# Revit family: 6218_Lange Gewindetülle mit Konus
name_source: partatom
category: Rohrformteile
units: mm (PartAtom-declared; Revit-internal decimal feet)

## family parameters
Arbeitsebenenbasiert = Nein
Beim Laden mit Abzugskörper schneiden = Nein
Bemaßung runder Anschluss = Durchmesser verwenden
Gemeinsam genutzt = Nein
Immer vertikal = Ja
OmniClass-Nummer = 23.65.55.14
OmniClass-Titel = Valves for Liquid Services
Teiletyp = Verbindung

## types (3) — shared parameters
Ausführung = Lange Gewindetülle, ohne Mutter, mit Konus, zum ausgleichen von Baumaßdifferenzen
Gewindetülle = Messing CW614N, vernickelt
Hersteller = HERZ Armaturen Ges.m.b.H.
Hinweiß = Der O-Ring dient als zusätzliche Dichtung, bei Verlust ist die Gewindetülle metallisch dichtend.
L02 = 3 mm  [stored 0.00984252 ft]
Max. Betriebsdruck = 1000000.0 Pa
Max. Betriebstemperatur = 110 °C
Medium = Heizungswasser nach ÖNORM H5195 oder VDI- Richtlinie 2035.
Die Verwendung von Ethylen- oder Propyleneglykol in einem Mischungsverhältnis 25- 50% ist zulässig.
O-Ring = EPDM
SCRNCODE = 07;01;01
SCRNSEQ = AWI;AWI_TYP="1001";1
URL = www.herz-armaturen.at
zero-valued in all types: Vorgabe-Ansicht

## per-type parameters (varying)
| type | D00 | D01 | D02 | D03 | D04 | L00 | L01 | L03 | Nennweite | R01 |
| G3/8 x 40mm | 10 mm  [stored 0.0328084 ft] | 9 mm  [stored 0.0295276 ft] | 7 mm  [stored 0.0229659 ft] | 8 mm  [stored 0.0262467 ft] | 5 mm  [stored 0.0164042 ft] | 40 mm  [stored 0.131234 ft] | 7 mm  [stored 0.0229659 ft] | 30 mm | 10 mm  [stored 0.0328084 ft] | 9 mm  [stored 0.0295276 ft] |
| G1/2 x 76mm | 12 mm  [stored 0.0393701 ft] | 11 mm | 9 mm  [stored 0.0295276 ft] | 10 mm  [stored 0.0328084 ft] | 8 mm  [stored 0.0262467 ft] | 76 mm  [stored 0.249344 ft] | 8 mm  [stored 0.0262467 ft] | 63 mm  [stored 0.206693 ft] | 15 mm  [stored 0.0492126 ft] | 11 mm |
| G3/4 x 70mm | 15 mm  [stored 0.0492126 ft] | 14 mm  [stored 0.0459318 ft] | 12 mm  [stored 0.0393701 ft] | 13 mm | 10 mm  [stored 0.0328084 ft] | 70 mm  [stored 0.229659 ft] | 9 mm  [stored 0.0295276 ft] | 56 mm  [stored 0.183727 ft] | 20 mm  [stored 0.0656168 ft] | 15 mm  [stored 0.0492126 ft] |

note: [stored X ft] marks values corroborated as IEEE doubles in the binary element streams (Revit-internal decimal feet)
